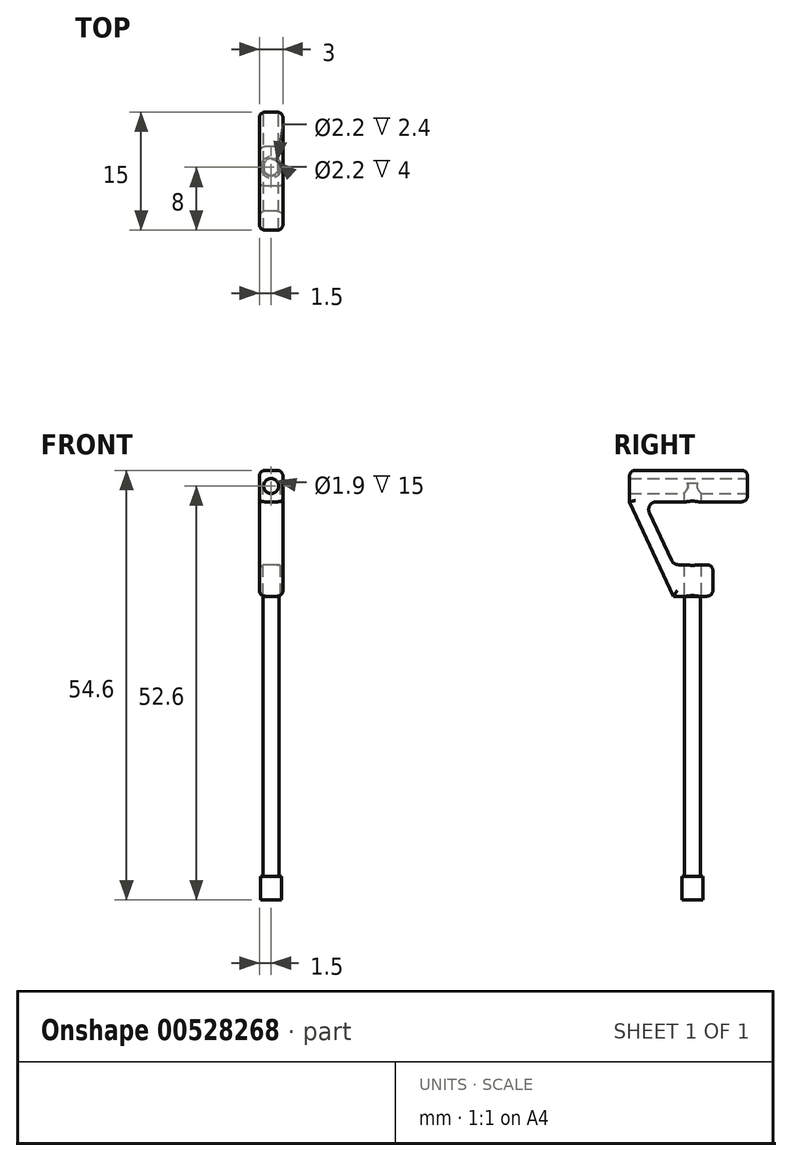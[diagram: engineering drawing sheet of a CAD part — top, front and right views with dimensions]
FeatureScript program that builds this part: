
annotation { "Feature Type Name" : "Feature", "Feature Type Description" : "" }
export const myFeature = defineFeature(function(context is Context, id is Id, definition is map)
    precondition{}
    {
        {
            var Q0;
            Q0=qCreatedBy(makeId("Top.planeOp"),FACE);
            var sketch = newSketch(context, id + "F0", { "sketchPlane" : qUnion([Q0])});
            skCircle(sketch, "E0", {"center": v(0, 0) * mm, "radius": 1.35 * mm});
            skSolve(sketch);
        }
        {
            var Q0;
            Q0 = qSketchRegion(id + "F0", true);
            extrude(context, id + "F1", {"entities" : qUnion([Q0]), "depth" : 3 * mm, "offsetDistance" : 25 * mm});
        }
        {
            var Q0;
            Q0=makeQuery(id+"F1.opExtrude","CAP_FACE",FACE,{"disambiguationData":[OSD([sQuery(id+"F0.wireOp",EDGE,"E0")])],"isStart":false});
            var sketch = newSketch(context, id + "F2", { "sketchPlane" : qUnion([Q0])});
            skCircle(sketch, "E1", {"center": v(0, 0) * mm, "radius": 1 * mm});
            skSolve(sketch);
        }
        {
            var Q0;
            Q0 = qSketchRegion(id + "F2", true);
            extrude(context, id + "F3", {"entities" : qUnion([Q0]), "operationType" : NewBodyOperationType.ADD, "depth" : 50 * mm, "offsetDistance" : 25 * mm});
        }
        {
            var Q0;
            Q0=qCreatedBy(makeId("Right.planeOp"),FACE);
            var sketch = newSketch(context, id + "F4", { "sketchPlane" : qUnion([Q0])});
            skLineSegment(sketch, "E2.bottom", {"start": v(7, 54.6) * mm, "end": v(-8, 54.6) * mm});
            skLineSegment(sketch, "E2.top", {"start": v(7, 50.6) * mm, "end": v(-8, 50.6) * mm});
            skLineSegment(sketch, "E2.left", {"start": v(7, 54.6) * mm, "end": v(7, 50.6) * mm});
            skLineSegment(sketch, "E2.right", {"start": v(-8, 54.6) * mm, "end": v(-8, 50.6) * mm});
            skLineSegment(sketch, "E3", {"start": v(-1, 3) * mm, "end": v(-1, 53) * mm, "construction": true});
            skLineSegment(sketch, "E4", {"start": v(1, 53) * mm, "end": v(1, 3) * mm, "construction": true});
            skLineSegment(sketch, "E5.bottom", {"start": v(2.6, 42.6) * mm, "end": v(-2.4, 42.6) * mm});
            skLineSegment(sketch, "E5.top", {"start": v(2.6, 38.6) * mm, "end": v(-2.4, 38.6) * mm});
            skLineSegment(sketch, "E5.left", {"start": v(2.6, 42.6) * mm, "end": v(2.6, 38.6) * mm});
            skLineSegment(sketch, "E5.right", {"start": v(-2.4, 42.6) * mm, "end": v(-2.4, 38.6) * mm});
            skLineSegment(sketch, "E6", {"start": v(-2.4, 42.6) * mm, "end": v(-6.13, 50.6) * mm});
            skLineSegment(sketch, "E7", {"start": v(-2.4, 38.6) * mm, "end": v(-8, 50.6) * mm});
            skSolve(sketch);
        }
        {
            var Q0;
            Q0=makeQuery(id+"F4.imprint","IMPRINT",FACE,{"disambiguationData":[TD([[makeQuery(id+"F4.imprint","IMPRINT",EDGE,{"derivedFrom":sQuery(id+"F4.wireOp",EDGE,"E2.bottom")}),1.0]])]});
            var Q1;
            Q1=makeQuery(id+"F4.imprint","IMPRINT",FACE,{"disambiguationData":[TD([[makeQuery(id+"F4.imprint","IMPRINT",EDGE,{"derivedFrom":sQuery(id+"F4.wireOp",EDGE,"E5.bottom")}),1.0]])]});
            var Q2;
            Q2=makeQuery(id+"F4.imprint","IMPRINT",FACE,{"disambiguationData":[TD([[makeQuery(id+"F4.imprint","IMPRINT",EDGE,{"derivedFrom":sQuery(id+"F4.wireOp",EDGE,"E5.right")}),-1.0]])]});
            extrude(context, id + "F5", {"entities" : qUnion([Q0, Q1, Q2]), "endBound" : BoundingType.SYMMETRIC, "depth" : 3 * mm, "offsetDistance" : 25 * mm});
        }
        {
            var Q0;
            Q0=makeQuery(id+"F5.opExtrude","SWEPT_FACE",FACE,{"disambiguationData":[OSD([sQuery(id+"F4.wireOp",EDGE,"E5.top")])]});
            var sketch = newSketch(context, id + "F6", { "sketchPlane" : qUnion([Q0])});
            skCircle(sketch, "E8.0", {"center": v(0, 0) * mm, "radius": 1 * mm, "construction": true});
            skCircle(sketch, "E9.0", {"center": v(0, 0) * mm, "radius": 1.1 * mm});
            skSolve(sketch);
        }
        {
            var Q0;
            Q0=makeQuery(id+"F6.imprint","IMPRINT",FACE,{"disambiguationData":[TD([[makeQuery(id+"F6.imprint","IMPRINT",EDGE,{"derivedFrom":sQuery(id+"F6.wireOp",EDGE,"E9.0")}),1.0]])]});
            var Q1;
            Q1=makeQuery(id+"F3.opExtrude","CAP_FACE",FACE,{"disambiguationData":[OSD([sQuery(id+"F2.wireOp",EDGE,"E1")])],"isStart":false});
            extrude(context, id + "F7", {"entities" : qUnion([Q0]), "operationType" : NewBodyOperationType.REMOVE, "endBound" : BoundingType.UP_TO_SURFACE, "oppositeDirection" : true, "depth" : 18.5 * mm, "endBoundEntityFace" : qUnion([Q1]), "offsetDistance" : 25 * mm});
        }
        {
            var Q0;
            Q0=makeQuery(id+"F5.opExtrude","SWEPT_FACE",FACE,{"disambiguationData":[OSD([sQuery(id+"F4.wireOp",EDGE,"E2.left")])]});
            var sketch = newSketch(context, id + "F8", { "sketchPlane" : qUnion([Q0])});
            skCircle(sketch, "E10", {"center": v(0, 52.6) * mm, "radius": 0.95 * mm});
            skLineSegment(sketch, "E11", {"start": v(0, 54.6) * mm, "end": v(0, 50.6) * mm, "construction": true});
            skSolve(sketch);
        }
        {
            var Q0;
            Q0=makeQuery(id+"F8.imprint","IMPRINT",FACE,{"disambiguationData":[TD([[makeQuery(id+"F8.imprint","IMPRINT",EDGE,{"derivedFrom":sQuery(id+"F8.wireOp",EDGE,"E10")}),1.0]])]});
            extrude(context, id + "F9", {"entities" : qUnion([Q0]), "operationType" : NewBodyOperationType.REMOVE, "oppositeDirection" : true, "depth" : 25 * mm, "offsetDistance" : 25 * mm});
        }
        {
            var Q0;
            Q0=makeQuery(id+"F5.opExtrude","SWEPT_EDGE",EDGE,{"disambiguationData":[OSD([sQuery(id+"F4.wireOp",EDGE,"E2.top"),sQuery(id+"F4.wireOp",EDGE,"E6")])]});
            var Q1;
            Q1=makeQuery(id+"F5.opExtrude","SWEPT_EDGE",EDGE,{"disambiguationData":[OSD([sQuery(id+"F4.wireOp",EDGE,"E5.bottom"),sQuery(id+"F4.wireOp",EDGE,"E5.right"),sQuery(id+"F4.wireOp",EDGE,"E6")])]});
            fillet(context, id + "F10", {"entities" : qUnion([Q0, Q1]), "radius" : 1 * mm, "tangentPropagation" : true, "allowEdgeOverflow" : false});
        }
        {
            var Q0;
            Q0=makeQuery(id+"F5.opExtrude","CAP_EDGE",EDGE,{"disambiguationData":[OSD([sQuery(id+"F4.wireOp",EDGE,"E5.left")])],"isStart":true});
            var Q1;
            Q1=makeQuery(id+"F5.opExtrude","CAP_EDGE",EDGE,{"disambiguationData":[OSD([sQuery(id+"F4.wireOp",EDGE,"E2.left")])],"isStart":true});
            var Q2;
            Q2=makeQuery(id+"F5.opExtrude","CAP_EDGE",EDGE,{"disambiguationData":[OSD([sQuery(id+"F4.wireOp",EDGE,"E5.right")])],"isStart":true});
            var Q3;
            Q3=makeQuery(id+"F5.opExtrude","CAP_EDGE",EDGE,{"disambiguationData":[OSD([sQuery(id+"F4.wireOp",EDGE,"E2.left")])],"isStart":false});
            var Q4;
            Q4=makeQuery(id+"F5.opExtrude","CAP_EDGE",EDGE,{"disambiguationData":[OSD([sQuery(id+"F4.wireOp",EDGE,"E5.left")])],"isStart":false});
            var Q5;
            Q5=makeQuery(id+"F5.opExtrude","CAP_EDGE",EDGE,{"disambiguationData":[OSD([sQuery(id+"F4.wireOp",EDGE,"E2.bottom")])],"isStart":true});
            var Q6;
            Q6=makeQuery(id+"F5.opExtrude","CAP_EDGE",EDGE,{"disambiguationData":[OSD([sQuery(id+"F4.wireOp",EDGE,"E2.top")])],"isStart":true});
            var Q7;
            Q7=makeQuery(id+"F5.opExtrude","CAP_EDGE",EDGE,{"disambiguationData":[OSD([sQuery(id+"F4.wireOp",EDGE,"E2.right")])],"isStart":true});
            var Q8;
            Q8=makeQuery(id+"F5.opExtrude","SWEPT_EDGE",EDGE,{"disambiguationData":[OSD([sQuery(id+"F4.wireOp",EDGE,"E2.bottom"),sQuery(id+"F4.wireOp",EDGE,"E2.right")])]});
            var Q9;
            Q9=makeQuery(id+"F5.opExtrude","CAP_EDGE",EDGE,{"disambiguationData":[OSD([sQuery(id+"F4.wireOp",EDGE,"E2.right")])],"isStart":false});
            var Q10;
            {var subQ0=sQuery(id+"F4.wireOp",EDGE,"E2.right");var subQ1=sQuery(id+"F4.wireOp",EDGE,"E2.left");var subQ2=sQuery(id+"F4.wireOp",EDGE,"E2.top");var subQ3=sQuery(id+"F4.wireOp",EDGE,"E2.bottom");Q10=makeQuery(id+"F3xgIR9EsfrLKBQ_3.boolean.opBoolean","MERGE",FACE,{"derivedFrom":[makeQuery(id+"F5.opExtrude","CAP_FACE",FACE,{"disambiguationData":[OSD([subQ3,subQ2,subQ1,subQ0])],"isStart":false}),makeQuery(id+"F5.opExtrude","CAP_FACE",FACE,{"disambiguationData":[OSD([sQuery(id+"F4.wireOp",EDGE,"E5.bottom"),sQuery(id+"F4.wireOp",EDGE,"E5.top"),sQuery(id+"F4.wireOp",EDGE,"E5.left"),sQuery(id+"F4.wireOp",EDGE,"E5.right")])],"isStart":false}),makeQuery(id+"F3xgIR9EsfrLKBQ_3.opExtrude","CAP_FACE",FACE,{"disambiguationData":[OSD([subQ3,subQ2,subQ1,subQ0])],"isStart":false})]});}
            var Q11;
            Q11=makeQuery(id+"F5.opExtrude","CAP_EDGE",EDGE,{"disambiguationData":[OSD([sQuery(id+"F4.wireOp",EDGE,"E7")])],"isStart":true});
            var Q12;
            Q12=makeQuery(id+"F5.opExtrude","CAP_EDGE",EDGE,{"disambiguationData":[OSD([sQuery(id+"F4.wireOp",EDGE,"E5.top")])],"isStart":true});
            var Q13;
            Q13=makeQuery(id+"F5.opExtrude","CAP_EDGE",EDGE,{"disambiguationData":[OSD([sQuery(id+"F4.wireOp",EDGE,"E5.bottom")])],"isStart":true});
            var Q14;
            Q14=makeQuery(id+"F5.opExtrude","CAP_EDGE",EDGE,{"disambiguationData":[OSD([sQuery(id+"F4.wireOp",EDGE,"E6")])],"isStart":true});
            var Q15;
            Q15=makeQuery(id+"F5.opExtrude","SWEPT_EDGE",EDGE,{"disambiguationData":[OSD([sQuery(id+"F4.wireOp",EDGE,"E2.bottom"),sQuery(id+"F4.wireOp",EDGE,"E2.left")])]});
            var Q16;
            Q16=makeQuery(id+"F5.opExtrude","SWEPT_EDGE",EDGE,{"disambiguationData":[OSD([sQuery(id+"F4.wireOp",EDGE,"E2.top"),sQuery(id+"F4.wireOp",EDGE,"E2.left")])]});
            var Q17;
            Q17=makeQuery(id+"F5.opExtrude","SWEPT_EDGE",EDGE,{"disambiguationData":[OSD([sQuery(id+"F4.wireOp",EDGE,"E5.top"),sQuery(id+"F4.wireOp",EDGE,"E5.left")])]});
            var Q18;
            Q18=makeQuery(id+"F5.opExtrude","SWEPT_EDGE",EDGE,{"disambiguationData":[OSD([sQuery(id+"F4.wireOp",EDGE,"E5.bottom"),sQuery(id+"F4.wireOp",EDGE,"E5.left")])]});
            fillet(context, id + "F11", {"entities" : qUnion([Q0, Q1, Q2, Q3, Q4, Q5, Q6, Q7, Q8, Q9, Q10, Q11, Q12, Q13, Q14, Q15, Q16, Q17, Q18]), "radius" : 0.75 * mm, "tangentPropagation" : true, "allowEdgeOverflow" : false});
        }
    });
